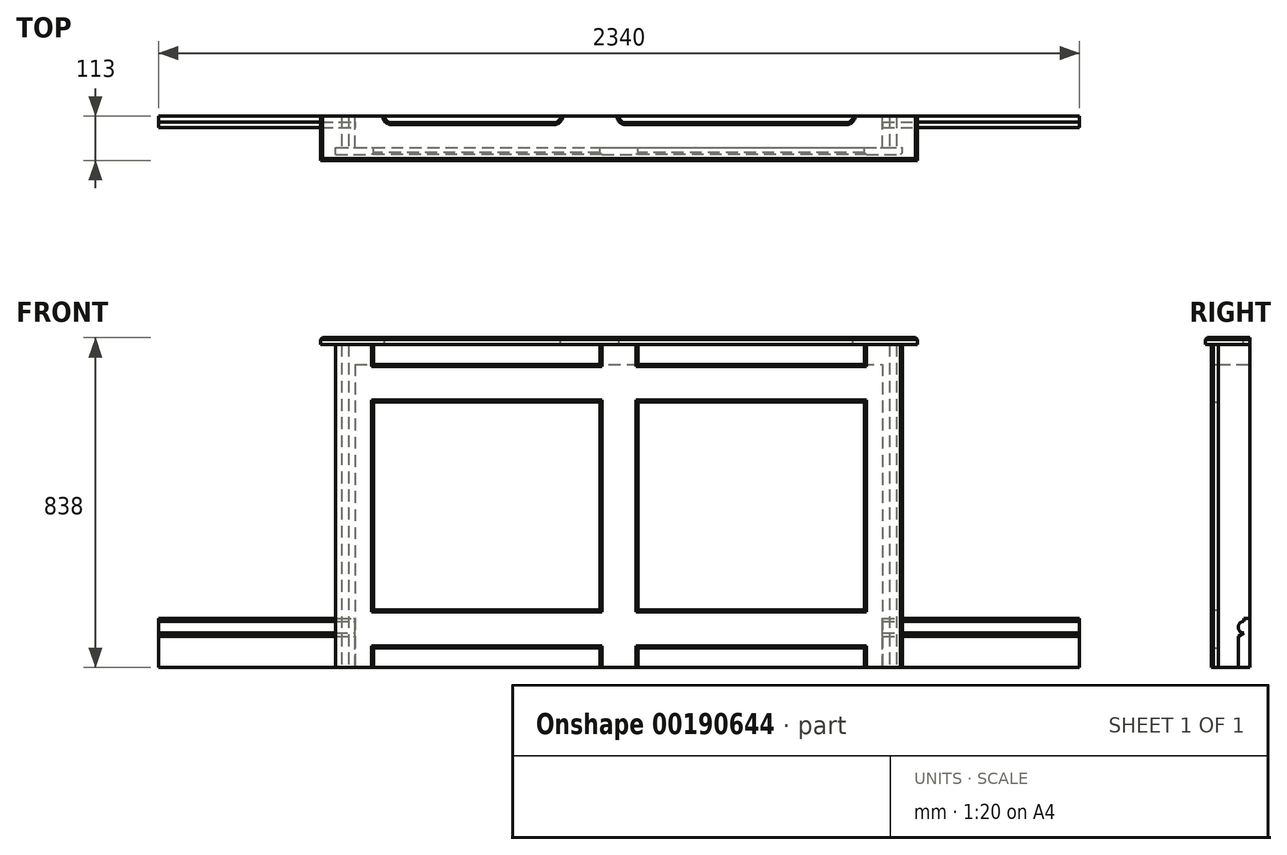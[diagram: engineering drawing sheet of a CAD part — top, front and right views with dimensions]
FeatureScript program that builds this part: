
annotation { "Feature Type Name" : "Feature", "Feature Type Description" : "" }
export const myFeature = defineFeature(function(context is Context, id is Id, definition is map)
    precondition{}
    {
        {
            var Q0;
            Q0=qCreatedBy(makeId("Top.planeOp"),FACE);
            var sketch = newSketch(context, id + "F0", { "sketchPlane" : qUnion([Q0])});
            skLineSegment(sketch, "E0.bottom", {"start": v(-60.17, -44.93) * mm, "end": v(1279.83, -44.93) * mm});
            skLineSegment(sketch, "E0.top", {"start": v(-60.17, 35.07) * mm, "end": v(1279.83, 35.07) * mm});
            skLineSegment(sketch, "E0.left", {"start": v(-60.17, -44.93) * mm, "end": v(-60.17, 35.07) * mm});
            skLineSegment(sketch, "E0.right", {"start": v(1279.83, -44.93) * mm, "end": v(1279.83, 35.07) * mm});
            skSolve(sketch);
        }
        {
            var Q0;
            Q0=makeQuery(id+"F0.imprint","IMPRINT",FACE,{"disambiguationData":[TD([[makeQuery(id+"F0.imprint","IMPRINT",EDGE,{"derivedFrom":sQuery(id+"F0.wireOp",EDGE,"E0.bottom")}),1.0]])]});
            extrude(context, id + "F1", {"entities" : qUnion([Q0]), "depth" : 770 * mm, "offsetDistance" : 25 * mm});
        }
        {
            var Q0;
            Q0=makeQuery(id+"F1.opExtrude","SWEPT_FACE",FACE,{"disambiguationData":[OSD([sQuery(id+"F0.wireOp",EDGE,"E0.left")])]});
            var sketch = newSketch(context, id + "F2", { "sketchPlane" : qUnion([Q0])});
            skLineSegment(sketch, "E1.bottom", {"start": v(-35.07, 0) * mm, "end": v(-5.07, 0) * mm});
            skLineSegment(sketch, "E1.top", {"start": v(-35.07, 125) * mm, "end": v(-20.25, 125) * mm});
            skLineSegment(sketch, "E1.left", {"start": v(-35.07, 0) * mm, "end": v(-35.07, 125) * mm});
            skLineSegment(sketch, "E2.right", {"start": v(-20.25, 125) * mm, "end": v(-20.25, 117.4) * mm});
            skArc(sketch, "E3", {"start": v(-20.25, 87.4) * mm, "mid": v(-5.25, 102.4) * mm, "end": v(-20.25, 117.4) * mm});
            skLineSegment(sketch, "E4", {"start": v(-20.25, 87.4) * mm, "end": v(-5.25, 78.73) * mm});
            skLineSegment(sketch, "E5", {"start": v(-5.25, 78.73) * mm, "end": v(-5.25, 0) * mm});
            skSolve(sketch);
        }
        {
            var Q0;
            Q0=makeQuery(id+"F2.imprint","IMPRINT",FACE,{"disambiguationData":[TD([[makeQuery(id+"F2.imprint","IMPRINT",EDGE,{"derivedFrom":sQuery(id+"F2.wireOp",EDGE,"E1.top")}),-1.0]])]});
            extrude(context, id + "F3", {"entities" : qUnion([Q0]), "operationType" : NewBodyOperationType.ADD, "depth" : 500 * mm, "offsetDistance" : 25 * mm, "hasSecondDirection" : true, "secondDirectionOppositeDirection" : true, "secondDirectionDepth" : 1840 * mm});
        }
        {
            var Q0;
            Q0=makeQuery(id+"F1.opExtrude","SWEPT_FACE",FACE,{"disambiguationData":[OSD([sQuery(id+"F0.wireOp",EDGE,"E0.bottom")])]});
            var sketch = newSketch(context, id + "F4", { "sketchPlane" : qUnion([Q0])});
            skLineSegment(sketch, "E6.0", {"start": v(561.83, 820) * mm, "end": v(561.83, 770) * mm});
            skLineSegment(sketch, "E7.0", {"start": v(657.83, 820) * mm, "end": v(657.83, 770) * mm});
            skLineSegment(sketch, "E8.0", {"start": v(-14.17, 50) * mm, "end": v(561.83, 50) * mm});
            skLineSegment(sketch, "E9.0", {"start": v(-14.17, 146) * mm, "end": v(561.83, 146) * mm});
            skLineSegment(sketch, "E10.0", {"start": v(1329.83, 820) * mm, "end": v(1329.83, 0) * mm});
            skLineSegment(sketch, "E11.0", {"start": v(-110.17, 820) * mm, "end": v(-110.17, 0) * mm});
            skLineSegment(sketch, "E12.0", {"start": v(-148.17, 820) * mm, "end": v(1367.83, 820) * mm});
            skLineSegment(sketch, "E13.0", {"start": v(-148.17, 838) * mm, "end": v(1367.83, 838) * mm});
            skLineSegment(sketch, "E14", {"start": v(-148.17, 838) * mm, "end": v(-148.17, 820) * mm});
            skLineSegment(sketch, "E15", {"start": v(1367.83, 838) * mm, "end": v(1367.83, 820) * mm});
            skLineSegment(sketch, "E16", {"start": v(561.83, 0) * mm, "end": v(657.83, 0) * mm});
            skLineSegment(sketch, "E17.0", {"start": v(1233.83, 820) * mm, "end": v(1233.83, 770) * mm});
            skLineSegment(sketch, "E18.0", {"start": v(-14.17, 820) * mm, "end": v(-14.17, 770) * mm});
            skLineSegment(sketch, "E19", {"start": v(-110.17, 0) * mm, "end": v(-14.17, 0) * mm});
            skLineSegment(sketch, "E20", {"start": v(1233.83, 0) * mm, "end": v(1329.83, 0) * mm});
            skLineSegment(sketch, "E21.trimOffspring", {"start": v(-14.17, 50) * mm, "end": v(-14.17, 0) * mm});
            skLineSegment(sketch, "E22.trimOffspring", {"start": v(657.83, 146) * mm, "end": v(1233.83, 146) * mm});
            skLineSegment(sketch, "E23.trimOffspring", {"start": v(657.83, 50) * mm, "end": v(1233.83, 50) * mm});
            skLineSegment(sketch, "E24.trimOffspring", {"start": v(561.83, 50) * mm, "end": v(561.83, 0) * mm});
            skLineSegment(sketch, "E25.trimOffspring", {"start": v(657.83, 50) * mm, "end": v(657.83, 0) * mm});
            skLineSegment(sketch, "E26.trimOffspring", {"start": v(1233.83, 50) * mm, "end": v(1233.83, 0) * mm});
            skLineSegment(sketch, "E27.0", {"start": v(-14.17, 674) * mm, "end": v(561.83, 674) * mm});
            skLineSegment(sketch, "E28.0", {"start": v(657.83, 674) * mm, "end": v(1233.83, 674) * mm});
            skLineSegment(sketch, "E29.0", {"start": v(-14.17, 770) * mm, "end": v(561.83, 770) * mm});
            skLineSegment(sketch, "E30.0", {"start": v(657.83, 770) * mm, "end": v(1233.83, 770) * mm});
            skLineSegment(sketch, "E31.trimOffspring", {"start": v(-14.17, 674) * mm, "end": v(-14.17, 146) * mm});
            skLineSegment(sketch, "E32.trimOffspring", {"start": v(561.83, 674) * mm, "end": v(561.83, 146) * mm});
            skLineSegment(sketch, "E33.trimOffspring", {"start": v(657.83, 674) * mm, "end": v(657.83, 146) * mm});
            skLineSegment(sketch, "E34.trimOffspring", {"start": v(1233.83, 674) * mm, "end": v(1233.83, 146) * mm});
            skLineSegment(sketch, "E35.0", {"start": v(-95.17, 820) * mm, "end": v(-95.17, 0) * mm});
            skLineSegment(sketch, "E36.0", {"start": v(-77.17, 820) * mm, "end": v(-77.17, 0) * mm});
            skLineSegment(sketch, "E37.0", {"start": v(1314.83, 820) * mm, "end": v(1314.83, 0) * mm});
            skLineSegment(sketch, "E38.0", {"start": v(1296.83, 820) * mm, "end": v(1296.83, 0) * mm});
            skSolve(sketch);
        }
        {
            var Q0;
            {var subQ2=sQuery(id+"F4.wireOp",EDGE,"E11.0");Q0=makeQuery(id+"F4.imprint","IMPRINT",FACE,{"disambiguationData":[TD([[makeQuery(id+"F4.imprint","IMPRINT",EDGE,{"derivedFrom":subQ2}),1.0]])]});}
            var Q1;
            Q1=makeQuery(id+"F4.imprint","IMPRINT",FACE,{"disambiguationData":[TD([[makeQuery(id+"F4.imprint","IMPRINT",EDGE,{"derivedFrom":sQuery(id+"F4.wireOp",EDGE,"E8.0")}),1.0]])]});
            var Q2;
            {var subQ0=sQuery(id+"F4.wireOp",EDGE,"E6.0");Q2=makeQuery(id+"F4.imprint","IMPRINT",FACE,{"disambiguationData":[TD([[makeQuery(id+"F4.imprint","IMPRINT",EDGE,{"derivedFrom":subQ0}),1.0]])]});}
            var Q3;
            {var subQ2=sQuery(id+"F4.wireOp",EDGE,"E10.0");Q3=makeQuery(id+"F4.imprint","IMPRINT",FACE,{"disambiguationData":[TD([[makeQuery(id+"F4.imprint","IMPRINT",EDGE,{"derivedFrom":subQ2}),-1.0]])]});}
            var Q4;
            {var subQ4=sQuery(id+"F4.wireOp",EDGE,"E18.0");Q4=makeQuery(id+"F4.imprint","IMPRINT",FACE,{"disambiguationData":[TD([[makeQuery(id+"F4.imprint","IMPRINT",EDGE,{"derivedFrom":subQ4}),-1.0]])]});}
            var Q5;
            {var subQ0=sQuery(id+"F4.wireOp",EDGE,"E35.0");Q5=makeQuery(id+"F4.imprint","IMPRINT",FACE,{"disambiguationData":[TD([[makeQuery(id+"F4.imprint","IMPRINT",EDGE,{"derivedFrom":subQ0}),1.0]])]});}
            var Q6;
            {var subQ4=sQuery(id+"F4.wireOp",EDGE,"E17.0");Q6=makeQuery(id+"F4.imprint","IMPRINT",FACE,{"disambiguationData":[TD([[makeQuery(id+"F4.imprint","IMPRINT",EDGE,{"derivedFrom":subQ4}),1.0]])]});}
            var Q7;
            {var subQ0=sQuery(id+"F4.wireOp",EDGE,"E37.0");Q7=makeQuery(id+"F4.imprint","IMPRINT",FACE,{"disambiguationData":[TD([[makeQuery(id+"F4.imprint","IMPRINT",EDGE,{"derivedFrom":subQ0}),-1.0]])]});}
            extrude(context, id + "F5", {"entities" : qUnion([Q0, Q1, Q2, Q3, Q4, Q5, Q6, Q7]), "depth" : 18 * mm, "offsetDistance" : 25 * mm});
        }
        {
            var Q0;
            Q0=makeQuery(id+"F5.opExtrude","CAP_EDGE",EDGE,{"disambiguationData":[OSD([sQuery(id+"F4.wireOp",EDGE,"E18.0")])],"isStart":false});
            var Q1;
            Q1=makeQuery(id+"F5.opExtrude","CAP_EDGE",EDGE,{"disambiguationData":[OSD([sQuery(id+"F4.wireOp",EDGE,"E29.0")])],"isStart":false});
            var Q2;
            Q2=makeQuery(id+"F5.opExtrude","CAP_EDGE",EDGE,{"disambiguationData":[OSD([sQuery(id+"F4.wireOp",EDGE,"E6.0")])],"isStart":false});
            var Q3;
            Q3=makeQuery(id+"F5.opExtrude","CAP_EDGE",EDGE,{"disambiguationData":[OSD([sQuery(id+"F4.wireOp",EDGE,"E7.0")])],"isStart":false});
            var Q4;
            Q4=makeQuery(id+"F5.opExtrude","CAP_EDGE",EDGE,{"disambiguationData":[OSD([sQuery(id+"F4.wireOp",EDGE,"E30.0")])],"isStart":false});
            var Q5;
            Q5=makeQuery(id+"F5.opExtrude","CAP_EDGE",EDGE,{"disambiguationData":[OSD([sQuery(id+"F4.wireOp",EDGE,"E17.0")])],"isStart":false});
            var Q6;
            Q6=makeQuery(id+"F5.opExtrude","CAP_EDGE",EDGE,{"disambiguationData":[OSD([sQuery(id+"F4.wireOp",EDGE,"E34.trimOffspring")])],"isStart":false});
            var Q7;
            Q7=makeQuery(id+"F5.opExtrude","CAP_EDGE",EDGE,{"disambiguationData":[OSD([sQuery(id+"F4.wireOp",EDGE,"E28.0")])],"isStart":false});
            var Q8;
            Q8=makeQuery(id+"F5.opExtrude","CAP_EDGE",EDGE,{"disambiguationData":[OSD([sQuery(id+"F4.wireOp",EDGE,"E33.trimOffspring")])],"isStart":false});
            var Q9;
            Q9=makeQuery(id+"F5.opExtrude","CAP_EDGE",EDGE,{"disambiguationData":[OSD([sQuery(id+"F4.wireOp",EDGE,"E22.trimOffspring")])],"isStart":false});
            var Q10;
            Q10=makeQuery(id+"F5.opExtrude","CAP_EDGE",EDGE,{"disambiguationData":[OSD([sQuery(id+"F4.wireOp",EDGE,"E32.trimOffspring")])],"isStart":false});
            var Q11;
            Q11=makeQuery(id+"F5.opExtrude","CAP_EDGE",EDGE,{"disambiguationData":[OSD([sQuery(id+"F4.wireOp",EDGE,"E27.0")])],"isStart":false});
            var Q12;
            Q12=makeQuery(id+"F5.opExtrude","CAP_EDGE",EDGE,{"disambiguationData":[OSD([sQuery(id+"F4.wireOp",EDGE,"E31.trimOffspring")])],"isStart":false});
            var Q13;
            Q13=makeQuery(id+"F5.opExtrude","CAP_EDGE",EDGE,{"disambiguationData":[OSD([sQuery(id+"F4.wireOp",EDGE,"E9.0")])],"isStart":false});
            var Q14;
            Q14=makeQuery(id+"F5.opExtrude","CAP_EDGE",EDGE,{"disambiguationData":[OSD([sQuery(id+"F4.wireOp",EDGE,"E21.trimOffspring")])],"isStart":false});
            var Q15;
            Q15=makeQuery(id+"F5.opExtrude","CAP_EDGE",EDGE,{"disambiguationData":[OSD([sQuery(id+"F4.wireOp",EDGE,"E8.0")])],"isStart":false});
            var Q16;
            Q16=makeQuery(id+"F5.opExtrude","CAP_EDGE",EDGE,{"disambiguationData":[OSD([sQuery(id+"F4.wireOp",EDGE,"E24.trimOffspring")])],"isStart":false});
            var Q17;
            Q17=makeQuery(id+"F5.opExtrude","CAP_EDGE",EDGE,{"disambiguationData":[OSD([sQuery(id+"F4.wireOp",EDGE,"E25.trimOffspring")])],"isStart":false});
            var Q18;
            Q18=makeQuery(id+"F5.opExtrude","CAP_EDGE",EDGE,{"disambiguationData":[OSD([sQuery(id+"F4.wireOp",EDGE,"E23.trimOffspring")])],"isStart":false});
            var Q19;
            Q19=makeQuery(id+"F5.opExtrude","CAP_EDGE",EDGE,{"disambiguationData":[OSD([sQuery(id+"F4.wireOp",EDGE,"E26.trimOffspring")])],"isStart":false});
            var Q20;
            Q20=makeQuery(id+"F5.opExtrude","CAP_EDGE",EDGE,{"disambiguationData":[OSD([sQuery(id+"F4.wireOp",EDGE,"E10.0")])],"isStart":false});
            chamfer(context, id + "F6", {"entities" : qUnion([Q0, Q1, Q2, Q3, Q4, Q5, Q6, Q7, Q8, Q9, Q10, Q11, Q12, Q13, Q14, Q15, Q16, Q17, Q18, Q19, Q20]), "width" : 5 * mm, "tangentPropagation" : true});
        }
        {
            var Q0;
            Q0=makeQuery(id+"F4.imprint","IMPRINT",FACE,{"disambiguationData":[TD([[makeQuery(id+"F4.imprint","IMPRINT",EDGE,{"derivedFrom":sQuery(id+"F4.wireOp",EDGE,"E13.0")}),-1.0]])]});
            extrude(context, id + "F7", {"entities" : qUnion([Q0]), "oppositeDirection" : true, "depth" : 63 * mm, "offsetDistance" : 25 * mm, "hasSecondDirection" : true, "secondDirectionOppositeDirection" : false, "secondDirectionDepth" : 33 * mm});
        }
        {
            var Q0;
            Q0=makeQuery(id+"F7.opExtrude","SWEPT_EDGE",EDGE,{"disambiguationData":[OSD([sQuery(id+"F4.wireOp",EDGE,"E13.0"),sQuery(id+"F4.wireOp",EDGE,"E14")])]});
            var Q1;
            Q1=makeQuery(id+"F7.opExtrude","CAP_EDGE",EDGE,{"disambiguationData":[OSD([sQuery(id+"F4.wireOp",EDGE,"E13.0")])],"isStart":true});
            var Q2;
            Q2=makeQuery(id+"F7.opExtrude","SWEPT_EDGE",EDGE,{"disambiguationData":[OSD([sQuery(id+"F4.wireOp",EDGE,"E13.0"),sQuery(id+"F4.wireOp",EDGE,"E15")])]});
            chamfer(context, id + "F8", {"entities" : qUnion([Q0, Q1, Q2]), "width" : 5 * mm, "tangentPropagation" : true});
        }
        {
            var Q0;
            {var subQ0=sQuery(id+"F4.wireOp",EDGE,"E35.0");Q0=makeQuery(id+"F4.imprint","IMPRINT",FACE,{"disambiguationData":[TD([[makeQuery(id+"F4.imprint","IMPRINT",EDGE,{"derivedFrom":subQ0}),1.0]])]});}
            var Q1;
            {var subQ0=sQuery(id+"F4.wireOp",EDGE,"E37.0");Q1=makeQuery(id+"F4.imprint","IMPRINT",FACE,{"disambiguationData":[TD([[makeQuery(id+"F4.imprint","IMPRINT",EDGE,{"derivedFrom":subQ0}),-1.0]])]});}
            extrude(context, id + "F9", {"entities" : qUnion([Q0, Q1]), "oppositeDirection" : true, "depth" : 80 * mm, "offsetDistance" : 25 * mm});
        }
        {
            var Q0;
            Q0=makeQuery(id+"F7.opExtrude","SWEPT_FACE",FACE,{"disambiguationData":[OSD([sQuery(id+"F4.wireOp",EDGE,"E13.0")])]});
            var sketch = newSketch(context, id + "F10", { "sketchPlane" : qUnion([Q0])});
            skPoint(sketch, "E39.0", {"position": v(-148.17, 18.07) * mm});
            skPoint(sketch, "E40.0", {"position": v(1367.83, 18.07) * mm});
            skLineSegment(sketch, "E41.0", {"start": v(-560.17, 35.07) * mm, "end": v(-60.17, 35.07) * mm});
            skLineSegment(sketch, "E41.1", {"start": v(1279.83, 35.07) * mm, "end": v(1779.83, 35.07) * mm});
            skLineSegment(sketch, "E42", {"start": v(-148.17, 18.07) * mm, "end": v(-148.17, 35.07) * mm});
            skLineSegment(sketch, "E43.0", {"start": v(757.83, 18.07) * mm, "end": v(757.83, 35.07) * mm});
            skLineSegment(sketch, "E44", {"start": v(1367.83, 18.07) * mm, "end": v(1367.83, 35.07) * mm});
            skLineSegment(sketch, "E45", {"start": v(14.83, 35.07) * mm, "end": v(31.83, 35.07) * mm});
            skCircle(sketch, "E46", {"center": v(31.83, 35.07) * mm, "radius": 17 * mm});
            skLineSegment(sketch, "E47", {"start": v(461.83, 35.07) * mm, "end": v(444.83, 35.07) * mm});
            skLineSegment(sketch, "E48", {"start": v(609.83, 35.07) * mm, "end": v(626.83, 35.07) * mm});
            skCircle(sketch, "E49", {"center": v(444.83, 35.07) * mm, "radius": 17 * mm});
            skCircle(sketch, "E50", {"center": v(626.83, 35.07) * mm, "radius": 17 * mm});
            skLineSegment(sketch, "E51", {"start": v(1204.83, 35.07) * mm, "end": v(1187.83, 35.07) * mm});
            skCircle(sketch, "E52", {"center": v(1187.83, 35.07) * mm, "radius": 17 * mm});
            skLineSegment(sketch, "E53", {"start": v(461.83, 35.07) * mm, "end": v(609.83, 35.07) * mm});
            skLineSegment(sketch, "E54", {"start": v(-148.17, 35.07) * mm, "end": v(14.83, 35.07) * mm});
            skLineSegment(sketch, "E55", {"start": v(1367.83, 35.07) * mm, "end": v(1204.83, 35.07) * mm});
            skLineSegment(sketch, "E56", {"start": v(-148.17, 18.07) * mm, "end": v(1367.83, 18.07) * mm});
            skSolve(sketch);
        }
        {
            var Q0;
            {var subQ3=sQuery(id+"F10.wireOp",EDGE,"E42");Q0=makeQuery(id+"F10.imprint","IMPRINT",FACE,{"disambiguationData":[TD([[makeQuery(id+"F10.imprint","IMPRINT",EDGE,{"derivedFrom":subQ3}),-1.0]])]});}
            var Q1;
            {var subQ0=sQuery(id+"F10.wireOp",EDGE,"E53");Q1=makeQuery(id+"F10.imprint","IMPRINT",FACE,{"disambiguationData":[TD([[makeQuery(id+"F10.imprint","IMPRINT",EDGE,{"derivedFrom":subQ0}),-1.0]])]});}
            var Q2;
            {var subQ3=sQuery(id+"F10.wireOp",EDGE,"E44");Q2=makeQuery(id+"F10.imprint","IMPRINT",FACE,{"disambiguationData":[TD([[makeQuery(id+"F10.imprint","IMPRINT",EDGE,{"derivedFrom":subQ3}),1.0]])]});}
            extrude(context, id + "F11", {"entities" : qUnion([Q0, Q1, Q2]), "operationType" : NewBodyOperationType.ADD, "oppositeDirection" : true, "depth" : 18 * mm, "offsetDistance" : 25 * mm});
        }
        {
            var Q0;
            Q0=makeQuery(id+"F11.opExtrude","CAP_EDGE",EDGE,{"disambiguationData":[OSD([sQuery(id+"F10.wireOp",EDGE,"E44")])],"isStart":true});
            var Q1;
            Q1=makeQuery(id+"F11.opExtrude","CAP_EDGE",EDGE,{"disambiguationData":[OSD([sQuery(id+"F10.wireOp",EDGE,"E52")])],"isStart":true});
            var Q2;
            Q2=makeQuery(id+"F11.opExtrude","CAP_EDGE",EDGE,{"disambiguationData":[OSD([sQuery(id+"F10.wireOp",EDGE,"E49")])],"isStart":true});
            var Q3;
            Q3=makeQuery(id+"F11.opExtrude","CAP_EDGE",EDGE,{"disambiguationData":[OSD([sQuery(id+"F10.wireOp",EDGE,"E42")])],"isStart":true});
            chamfer(context, id + "F12", {"entities" : qUnion([Q0, Q1, Q2, Q3]), "width" : 5 * mm, "tangentPropagation" : true});
        }
    });
